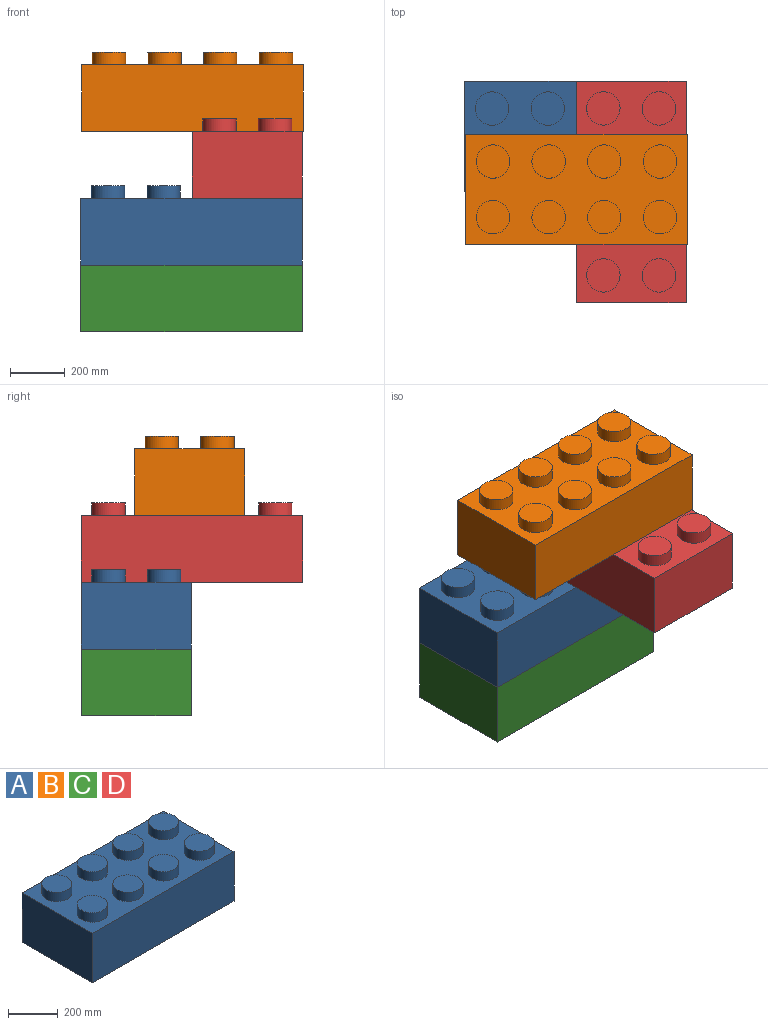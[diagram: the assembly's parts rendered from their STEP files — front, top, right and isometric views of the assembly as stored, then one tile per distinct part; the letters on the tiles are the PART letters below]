
ASSEMBLY  parts=4 mates=8
PART A: 39 faces, bbox 807.7x401.3x289.6 mm
  f0: plane 401.32x243.84mm, normal (-1,0,0), area 97857.9mm2, adj f1,f3,f4,f5
  f1: plane 807.72x243.84mm, normal (0,-1,0), area 196954.4mm2, adj f0,f2,f4,f5
  f2: plane 401.32x243.84mm, normal (1,0,0), area 97857.9mm2, adj f1,f3,f4,f5
  f3: plane 807.72x243.84mm, normal (0,1,0), area 196954.4mm2, adj f0,f2,f4,f5
  f4: plane 807.72x401.32mm, normal (0,0,1), area 230757.9mm2, adj f0,f1,f2,f3,f11,f13,f15,f17
  f5: plane 807.72x401.32mm, normal (0,0,-1), area 69987mm2, adj f0,f1,f2,f3,f6,f7,f8,f9
  f6: plane 340.36x213.36mm, normal (1,0,0), area 72619.2mm2, adj f5,f7,f9,f10
  f7: plane 746.76x213.36mm, normal (0,1,0), area 159328.7mm2, adj f5,f6,f8,f10
  f8: plane 340.36x213.36mm, normal (-1,0,0), area 72619.2mm2, adj f5,f7,f9,f10
  f9: plane 746.76x213.36mm, normal (0,-1,0), area 159328.7mm2, adj f5,f6,f8,f10
  f10: plane 746.76x340.36mm, normal (0,0,-1), area 189942.1mm2, adj f6,f7,f8,f9,f28,f32,f36
  f11: cylinder r=60.96mm len=121.92mm, axis (0,0,-1), area 17511.8mm2, adj f4,f12
  f12: plane 121.92x121.92mm, normal (0,0,1), area 11674.5mm2, adj f11
  f13: cylinder r=60.96mm len=121.92mm, axis (0,0,-1), area 17511.8mm2, adj f4,f14
  f14: plane 121.92x121.92mm, normal (0,0,1), area 11674.5mm2, adj f13
  f15: cylinder r=60.96mm len=121.92mm, axis (0,0,-1), area 17511.8mm2, adj f4,f16
  f16: plane 121.92x121.92mm, normal (0,0,1), area 11674.5mm2, adj f15
  f17: cylinder r=60.96mm len=121.92mm, axis (0,0,-1), area 17511.8mm2, adj f4,f18
  f18: plane 121.92x121.92mm, normal (0,0,1), area 11674.5mm2, adj f17
  f19: cylinder r=60.96mm len=121.92mm, axis (0,0,-1), area 17511.8mm2, adj f4,f20
  f20: plane 121.92x121.92mm, normal (0,0,1), area 11674.5mm2, adj f19
  f21: cylinder r=60.96mm len=121.92mm, axis (0,0,-1), area 17511.8mm2, adj f4,f22
  f22: plane 121.92x121.92mm, normal (0,0,1), area 11674.5mm2, adj f21
  f23: cylinder r=60.96mm len=121.92mm, axis (0,0,-1), area 17511.8mm2, adj f4,f24
  f24: plane 121.92x121.92mm, normal (0,0,1), area 11674.5mm2, adj f23
  f25: cylinder r=60.96mm len=121.92mm, axis (0,0,-1), area 17511.8mm2, adj f4,f26
  f26: plane 121.92x121.92mm, normal (0,0,1), area 11674.5mm2, adj f25
  f27: cylinder r=60.96mm len=213.36mm, axis (0,0,1), area 81721.8mm2, adj f29,f30
  f28: cylinder r=82.55mm len=213.36mm, axis (0,0,1), area 110664.9mm2, adj f10,f29
  f29: plane 165.1x165.1mm, normal (0,0,-1), area 9733.9mm2, adj f27,f28
  f30: plane 121.92x121.92mm, normal (0,0,-1), area 11674.5mm2, adj f27
  f31: cylinder r=60.96mm len=213.36mm, axis (0,0,1), area 81721.8mm2, adj f33,f34
  f32: cylinder r=82.55mm len=213.36mm, axis (0,0,1), area 110664.9mm2, adj f10,f33
  f33: plane 165.1x165.1mm, normal (0,0,-1), area 9733.9mm2, adj f31,f32
  f34: plane 121.92x121.92mm, normal (0,0,-1), area 11674.5mm2, adj f31
  f35: cylinder r=60.96mm len=213.36mm, axis (0,0,1), area 81721.8mm2, adj f37,f38
  f36: cylinder r=82.55mm len=213.36mm, axis (0,0,1), area 110664.9mm2, adj f10,f37
  f37: plane 165.1x165.1mm, normal (0,0,-1), area 9733.9mm2, adj f35,f36
  f38: plane 121.92x121.92mm, normal (0,0,-1), area 11674.5mm2, adj f35
PART B: same geometry as A
PART C: same geometry as A
PART D: same geometry as A
PLACE A t=(261.45,-268.96,287.51)mm
PLACE B t=(264.88,-463.23,775.19)mm
PLACE C t=(261.45,-268.96,43.67)mm fixed
PLACE D rot(axis=(0,0,1),90deg) t=(415.48,-525.81,531.35)mm
MATE planar C.f4 <-> A.f5  axis (0,0,1) through (667.55,-320.37,287.51)mm
MATE planar B.f31 <-> D.f4  axis (0,0,1) through (266.23,-523.57,775.19)mm
MATE planar D.f27 <-> D.f0  axis (0,0,-1) through (475.82,-726.39,531.35)mm
MATE planar B.f2 <-> B.f2  axis (1,0,0) through (670.98,-514.65,897.11)mm
MATE planar A.f4 <-> D.f31  axis (0,0,1) through (263.69,-320.37,531.35)mm
MATE planar A.f0 <-> C.f0  axis (-1,0,0) through (-140.17,-320.37,409.43)mm
MATE planar D.f1 <-> A.f2  axis (1,0,0) through (667.55,-523.57,653.27)mm
MATE planar D.f2 <-> A.f3  axis (0,1,0) through (466.89,-119.71,653.27)mm
